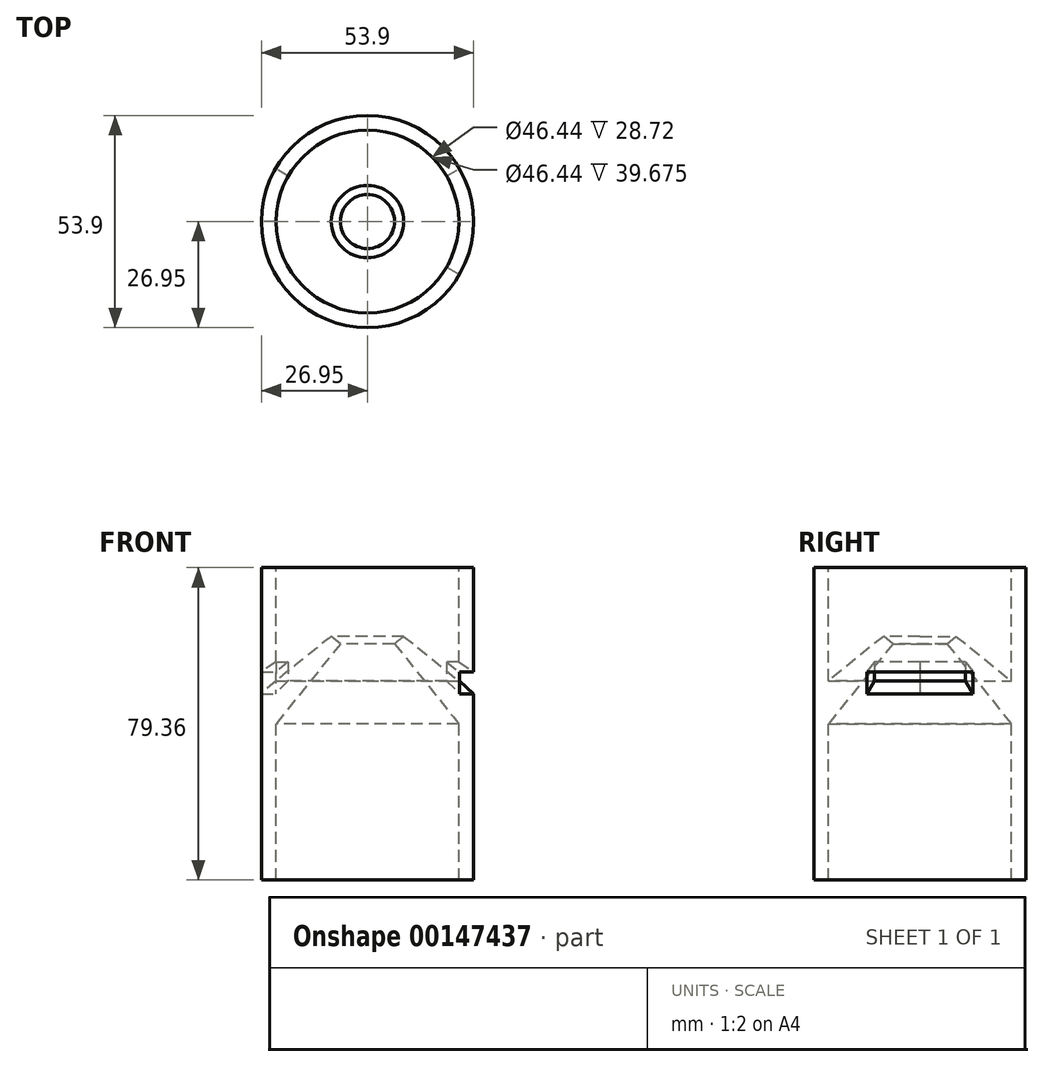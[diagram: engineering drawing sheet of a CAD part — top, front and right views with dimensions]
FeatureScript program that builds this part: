
annotation { "Feature Type Name" : "Feature", "Feature Type Description" : "" }
export const myFeature = defineFeature(function(context is Context, id is Id, definition is map)
    precondition{}
    {
        {
            var Q0;
            Q0=qCreatedBy(makeId("Front.planeOp"),FACE);
            var sketch = newSketch(context, id + "F0", { "sketchPlane" : qUnion([Q0])});
            skLineSegment(sketch, "E0", {"start": v(26.95, 39.68) * mm, "end": v(26.95, -39.68) * mm});
            skLineSegment(sketch, "E1", {"start": v(23.22, 39.68) * mm, "end": v(23.22, 10.96) * mm});
            skLineSegment(sketch, "E2", {"start": v(23.22, -39.68) * mm, "end": v(26.95, -39.68) * mm});
            skLineSegment(sketch, "E3", {"start": v(26.95, 39.68) * mm, "end": v(23.22, 39.68) * mm});
            skLineSegment(sketch, "E4", {"start": v(23.22, 0) * mm, "end": v(6.86, 20.37) * mm});
            skLineSegment(sketch, "E5", {"start": v(6.86, 20.37) * mm, "end": v(9.2, 22.25) * mm});
            skLineSegment(sketch, "E6", {"start": v(9.2, 22.25) * mm, "end": v(23.22, 10.96) * mm});
            skLineSegment(sketch, "E7.trimOffspring", {"start": v(23.22, 0) * mm, "end": v(23.22, -39.68) * mm});
            skLineSegment(sketch, "E8", {"start": v(0, 43.18) * mm, "end": v(0, -32.27) * mm});
            skLineSegment(sketch, "E9", {"start": v(23.22, 10.96) * mm, "end": v(26.95, 7.65) * mm});
            skLineSegment(sketch, "E10", {"start": v(23.22, 15.71) * mm, "end": v(26.95, 13.23) * mm});
            skSolve(sketch);
        }
        {
            var Q0;
            Q0 = qSketchRegion(id + "F0", true);
            var Q1;
            Q1=sQuery(id+"F0.wireOp",EDGE,"E8");
            revolve(context, id + "F1", {"entities" : qUnion([Q0]), "axis" : qUnion([Q1]), "revolveType" : RevolveType.FULL});
        }
        {
            var Q0;
            {var subQ0=sQuery(id+"F0.wireOp",EDGE,"E9");Q0=makeQuery(id+"F0.imprint","IMPRINT",FACE,{"disambiguationData":[TD([[makeQuery(id+"F0.imprint","IMPRINT",EDGE,{"derivedFrom":subQ0}),1.0]])]});}
            var Q1;
            Q1=sQuery(id+"F0.wireOp",EDGE,"E8");
            revolve(context, id + "F2", {"operationType" : NewBodyOperationType.REMOVE, "entities" : qUnion([Q0]), "axis" : qUnion([Q1]), "revolveType" : RevolveType.TWO_DIRECTIONS, "oppositeDirection" : true, "angle" : 30 * degree, "angleBack" : 330 * degree});
        }
        {
            var Q0;
            {var subQ0=sQuery(id+"F0.wireOp",EDGE,"E9");Q0=makeQuery(id+"F0.imprint","IMPRINT",FACE,{"disambiguationData":[TD([[makeQuery(id+"F0.imprint","IMPRINT",EDGE,{"derivedFrom":subQ0}),1.0]])]});}
            var Q1;
            Q1=sQuery(id+"F0.wireOp",EDGE,"E8");
            revolve(context, id + "F3", {"operationType" : NewBodyOperationType.REMOVE, "entities" : qUnion([Q0]), "axis" : qUnion([Q1]), "revolveType" : RevolveType.TWO_DIRECTIONS, "oppositeDirection" : true, "angle" : 180 * degree, "angleBack" : 150 * degree});
        }
    });
